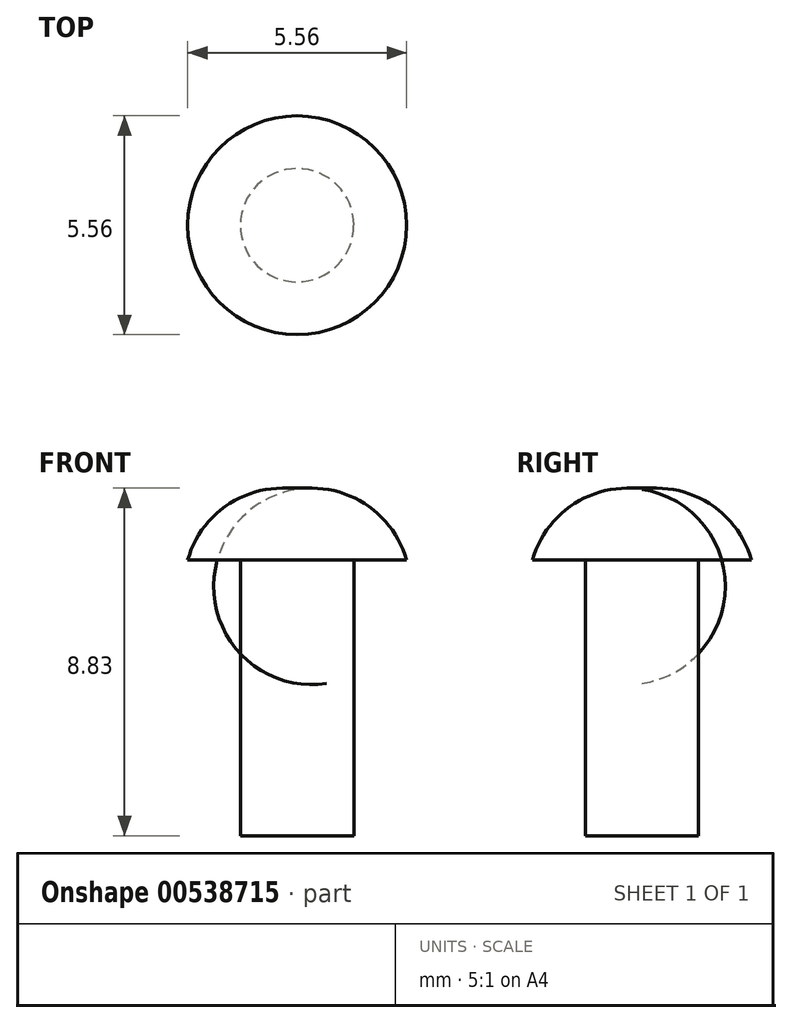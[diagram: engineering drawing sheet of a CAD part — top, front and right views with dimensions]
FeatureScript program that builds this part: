
annotation { "Feature Type Name" : "Feature", "Feature Type Description" : "" }
export const myFeature = defineFeature(function(context is Context, id is Id, definition is map)
    precondition{}
    {
        {
            var Q0;
            Q0=qCreatedBy(makeId("Front.planeOp"),FACE);
            var sketch = newSketch(context, id + "F0", { "sketchPlane" : qUnion([Q0])});
            skLineSegment(sketch, "E0", {"start": v(0, -7) * mm, "end": v(1.44, -7) * mm});
            skLineSegment(sketch, "E1", {"start": v(1.44, -7) * mm, "end": v(1.44, 0) * mm});
            skLineSegment(sketch, "E2", {"start": v(1.44, 0) * mm, "end": v(2.78, 0) * mm});
            skArc(sketch, "E3", {"start": v(2.78, 0) * mm, "mid": v(1.73, 1.43) * mm, "end": v(0, 1.8) * mm});
            skPoint(sketch, "E3.second.point", {"position": v(1.35, 1.63) * mm});
            skPoint(sketch, "E3.third.point", {"position": v(2.62, 0.42) * mm});
            skLineSegment(sketch, "E4", {"start": v(0, 1.8) * mm, "end": v(0, -7) * mm});
            skPoint(sketch, "E5.orphan", {"position": v(0, 2.86) * mm});
            skSolve(sketch);
        }
        {
            var Q0;
            Q0=makeQuery(id+"F0.imprint","IMPRINT",FACE,{"disambiguationData":[TD([[makeQuery(id+"F0.imprint","IMPRINT",EDGE,{"derivedFrom":sQuery(id+"F0.wireOp",EDGE,"E0")}),1.0]])]});
            var Q1;
            Q1=sQuery(id+"F0.wireOp",EDGE,"E4");
            revolve(context, id + "F1", {"entities" : qUnion([Q0]), "axis" : qUnion([Q1]), "revolveType" : RevolveType.FULL});
        }
    });
